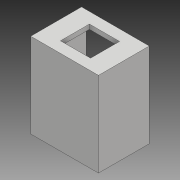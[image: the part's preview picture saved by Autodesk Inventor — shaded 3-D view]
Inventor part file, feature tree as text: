
AUTODESK INVENTOR PART (.ipt)
format: ipt  version: 2017 (Build 210142000, 142)  size: 92,160 bytes
history: native  units: mm
features: extrude x2, sketch x2, shell x1
ambient origin geometry x8: Origin, YZ Plane, XZ Plane, XY Plane, X Axis, Y Axis, Z Axis, Center Point
bodies: Solid1 (feature_tree)
feature tree (5):
  extrude  "Extrusion1"  Depth=150.0mm
  shell  "Shell1"  Thickness=90.0mm
  extrude  "Extrusion2"  Depth=53.362mm
  sketch  "Sketch1"  dims[d0=120.0mm d1=150.0mm d2=90.0mm d3=0.0mm]
  sketch  "Sketch2"  dims[d4=8.0mm d5=53.362mm d6=51.362mm d7=80.0mm d8=0.0mm]
